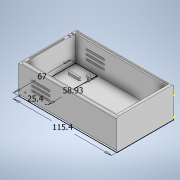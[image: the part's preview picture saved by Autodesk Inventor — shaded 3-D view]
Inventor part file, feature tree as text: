
AUTODESK INVENTOR PART (.ipt)
format: ipt  version: 2020.2 (Build 242310000, 310)  size: 407,552 bytes
history: native  units: mm
features: sketch x13, extrude x11, fillet x2, direct_edit x2, other x2, shell x1
ambient origin geometry x8: Origin, YZ Plane, XZ Plane, XY Plane, X Axis, Y Axis, Z Axis, Center Point
bodies: Solid1 (feature_tree)
feature tree (31):
  extrude  "Extrusion1"  Depth=67.0mm
  shell  "Shell1"  Thickness=25.0mm
  fillet  "Fillet1"  Radius=3.0mm
  sketch  "Sketch2"  dims[d11=2.0mm d12=10.0mm]
  direct_edit  "Direct Edit1"
  extrude  "Extrusion2"  Depth=10.0mm
  extrude  "Extrusion3"  Depth=1.5mm
  direct_edit  "Direct Edit2"
  sketch  "Sketch5"  dims[d17=113.75mm d18=0.0mm d19=10.0mm d20=0.0mm]
  extrude  "Extrusion6"  Depth=1.5mm
  extrude  "Extrusion7"  Depth=10.0mm TaperAngle=0.0deg
  extrude  "Extrusion8"  Depth=1.5mm
  extrude  "Extrusion9"  Depth=20.0mm
  fillet  "Fillet3"  Radius=1.25mm
  extrude  "Extrusion10"  Depth=3.0mm
  sketch  "Sketch17"  dims[d82=16.25mm d83=270.0deg]
  extrude  "Extrusion11"  Depth=4.0mm TaperAngle=0.0deg
  extrude  "Extrusion14"  TaperAngle=270.0deg  [1 undecoded]
  extrude  "Extrusion15"  TaperAngle=90.0deg  [1 undecoded]
  sketch  "Sketch1"  dims[d6=115.4mm d7=67.0mm d8=25.0mm d9=0.0mm d10=3.0mm]
  sketch  "Sketch3"  dims[d13=2.0mm d14=1.5mm]
  sketch  "Sketch4"  dims[d15=1.5mm d16=1.5mm]
  sketch  "Sketch11"  dims[d21=1.0mm d22=1.5mm]
  sketch  "Sketch12"  dims[d23=33.5mm d24=20.0mm d25=1.25mm]
  sketch  "Sketch14"  dims[d74=1.0mm d75=-11.34464mm d76=3.0mm]
  sketch  "Sketch16"  dims[d77=4.0mm d78=0.0mm d79=4.0mm d80=0.0mm]
  sketch  "Sketch18"  dims[d84=5.0mm d85=90.0deg]
  sketch  "Sketch19"  dims[d86=5.0mm]
  sketch  "Sketch21"  dims[d87=90.0deg d88=10.0mm d89=90.0deg d90=10.0mm d91=180.0deg d92=10.0mm d93=0.0mm d94=2.0mm d95=10.0mm d96=0.0mm d97=2.0mm d98=10.0mm d99=180.0deg d100=10.0mm d101=0.0mm d102=2.0mm d103=0.0mm d104=0.0mm d105=2.0mm d106=0.5mm d107=270.0deg d108=2.0mm d109=90.0deg d110=2.0mm d111=0.0mm d112=1.3mm d113=1.35mm d114=10.0mm d115=0.0mm d116=25.4mm d117=58.93mm d118=30.5mm d119=90.0deg d120=27.5mm d121=90.0deg d122=14.0mm d123=0.0mm d124=15.25mm d125=90.0deg d126=15.25mm d127=90.0deg d128=6.0mm d129=0.0mm d130=2.0mm d131=6.0mm d132=0.0mm d133=2.0mm d134=3.0mm d135=0.0mm d136=30.5mm d137=26.25mm d139=90.0deg d140=20.0mm d141=90.0deg d143=90.0deg d146=90.0deg d156=1.5mm d157=3.0mm d158=1.5mm d159=3.0mm d160=4.2mm d161=0.0mm d162=3.0mm d163=3.0mm d164=3.0mm d165=3.0mm d166=1.5mm d167=-2.617994mm d26=0.5mm d27=0.872665mm d28=0.5mm d29=0.872665mm d45=1.0mm d46=1.0mm d47=1.0mm d48=0.15mm d49=0.25mm d50=0.375mm d51=14.3117mm d52=0.75mm d53=20.594885mm d54=0.0625mm d55=0.75mm d56=0.375mm d66=1.0mm d67=1.0mm d68=1.0mm d69=0.15mm d70=0.25mm d71=0.375mm d72=14.3117mm d73=0.75mm d81=0.5mm]
  other  "Size1"
  other  "Size2"
note: 2 required parameter values undecoded (feature->parameter linkage not recoverable at this tier; creation-order binding heuristic only, values carry confidence <= 0.55)
